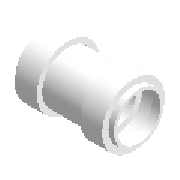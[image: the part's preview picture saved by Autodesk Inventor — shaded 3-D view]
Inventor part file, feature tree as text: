
AUTODESK INVENTOR PART (.ipt)
format: ipt  version: 2023 (Build 270158000, 158)  size: 194,560 bytes
history: native  units: mm (DEFAULTED — no unit token found)
features: other x8, revolve x1, sketch x1
ambient origin geometry x8: Origin, YZ Plane, XZ Plane, XY Plane, X Axis, Y Axis, Z Axis, Center Point
bodies: Solid1 (feature_tree)
feature tree (10):
  revolve  "Revolution1"  [1 undecoded]
  other  "Work Point1"
  other  "Work Point2"
  other  "Work Axis1"
  other  "Work Point3"
  other  "Work Axis2"
  other  "Work Point4"
  other  "Work Axis3"
  other  "Work Axis4"
  sketch  "Sketch1"  dims[d0=2.3mm d1=2.3mm d2=2.3mm d3=2.3mm d4=18.0mm d69=90.0deg d5=36.0mm d6=40.3mm d7=3.0mm d8=6.9mm d9=6.3mm]
note: 1 required parameter value undecoded (feature->parameter linkage not recoverable at this tier; creation-order binding heuristic only, values carry confidence <= 0.55)
